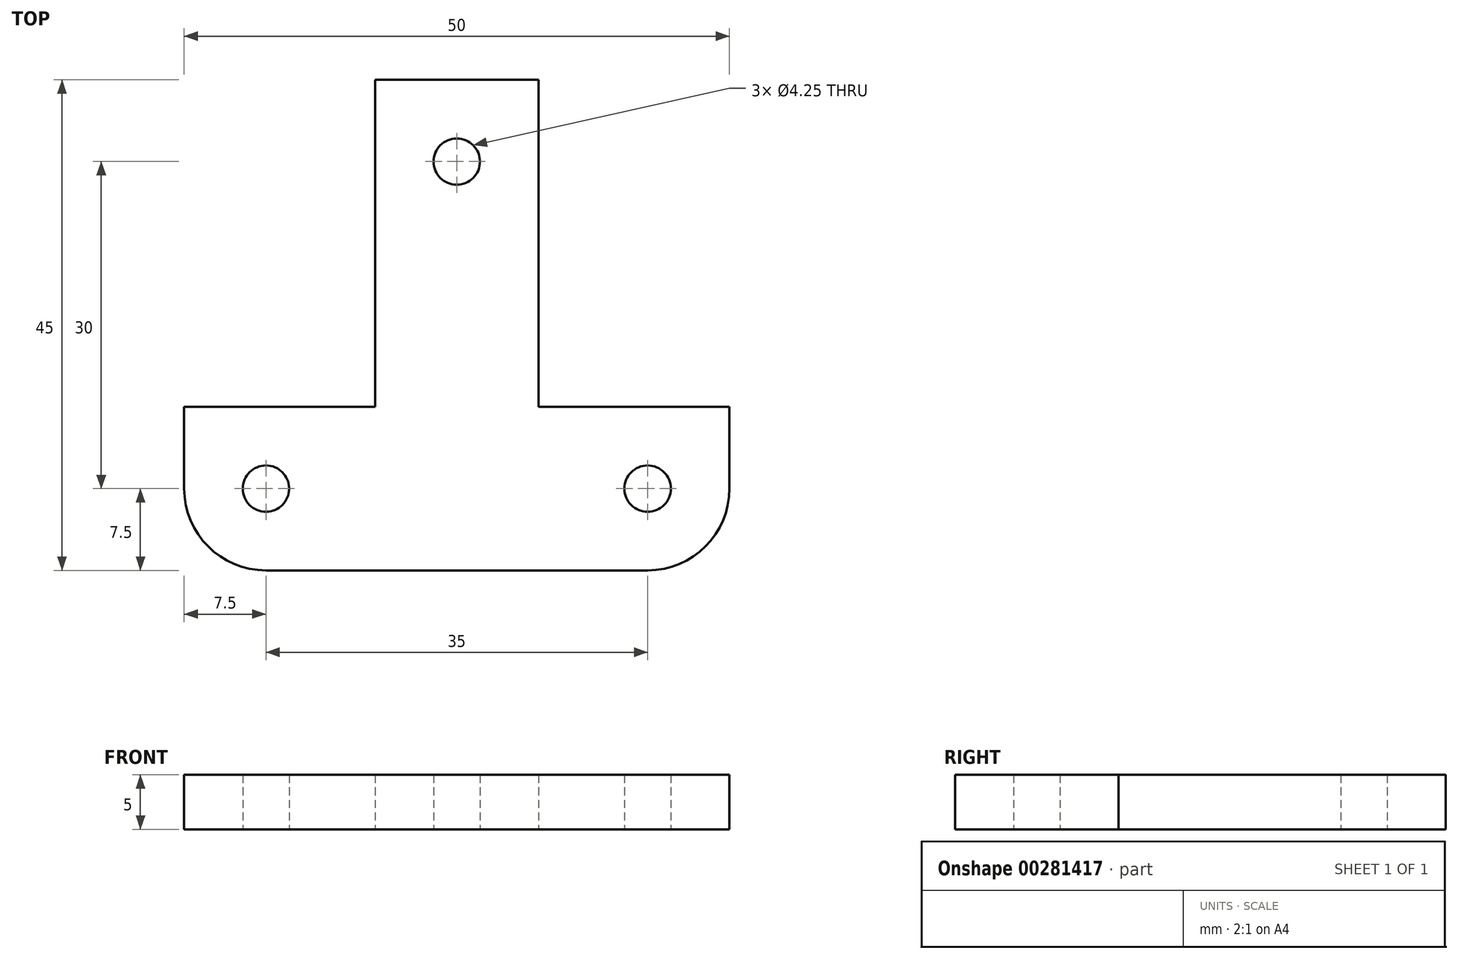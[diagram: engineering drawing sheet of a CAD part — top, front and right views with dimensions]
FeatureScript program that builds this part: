
annotation { "Feature Type Name" : "Feature", "Feature Type Description" : "" }
export const myFeature = defineFeature(function(context is Context, id is Id, definition is map)
    precondition{}
    {
        {
            var Q0;
            Q0=qCreatedBy(makeId("Top.planeOp"),FACE);
            var sketch = newSketch(context, id + "F0", { "sketchPlane" : qUnion([Q0])});
            skLineSegment(sketch, "E0", {"start": v(0, 37.5) * mm, "end": v(7.5, 37.5) * mm});
            skLineSegment(sketch, "E1", {"start": v(7.5, 37.5) * mm, "end": v(7.5, 7.5) * mm});
            skLineSegment(sketch, "E2", {"start": v(7.5, 7.5) * mm, "end": v(25, 7.5) * mm});
            skLineSegment(sketch, "E3", {"start": v(25, 7.5) * mm, "end": v(25, 0) * mm});
            skLineSegment(sketch, "E4.MirrorCS", {"start": v(0, 37.5) * mm, "end": v(-7.5, 37.5) * mm});
            skLineSegment(sketch, "E5.MirrorCS", {"start": v(-7.5, 37.5) * mm, "end": v(-7.5, 7.5) * mm});
            skLineSegment(sketch, "E6.MirrorCS", {"start": v(-7.5, 7.5) * mm, "end": v(-25, 7.5) * mm});
            skLineSegment(sketch, "E7.MirrorCS", {"start": v(-25, 7.5) * mm, "end": v(-25, 0) * mm});
            skLineSegment(sketch, "E8", {"start": v(-25, 0) * mm, "end": v(-25, -7.5) * mm});
            skLineSegment(sketch, "E9", {"start": v(-25, -7.5) * mm, "end": v(0, -7.5) * mm});
            skLineSegment(sketch, "E10.MirrorCS", {"start": v(25, -7.5) * mm, "end": v(0, -7.5) * mm});
            skLineSegment(sketch, "E11.MirrorCS", {"start": v(25, 0) * mm, "end": v(25, -7.5) * mm});
            skCircle(sketch, "E12", {"center": v(-17.5, 0) * mm, "radius": 2.12 * mm});
            skCircle(sketch, "E13", {"center": v(17.5, 0) * mm, "radius": 2.12 * mm});
            skCircle(sketch, "E14", {"center": v(0, 30) * mm, "radius": 2.12 * mm});
            skPoint(sketch, "E15.visualSharp", {"position": v(-7.5, 37.5) * mm});
            skLineSegment(sketch, "E15.filletArc", {"start": v(-7.5, 37.5) * mm, "end": v(-7.5, 37.5) * mm});
            skPoint(sketch, "E16.visualSharp", {"position": v(7.5, 37.5) * mm});
            skLineSegment(sketch, "E16.filletArc", {"start": v(7.5, 37.5) * mm, "end": v(7.5, 37.5) * mm});
            skPoint(sketch, "E17.visualSharp", {"position": v(-25, 7.5) * mm});
            skLineSegment(sketch, "E17.filletArc", {"start": v(-25, 7.5) * mm, "end": v(-25, 7.5) * mm});
            skPoint(sketch, "E18.visualSharp", {"position": v(-25, -7.5) * mm});
            skLineSegment(sketch, "E18.filletArc", {"start": v(-25, -7.5) * mm, "end": v(-25, -7.5) * mm});
            skPoint(sketch, "E19.visualSharp", {"position": v(25, -7.5) * mm});
            skLineSegment(sketch, "E19.filletArc", {"start": v(25, -7.5) * mm, "end": v(25, -7.5) * mm});
            skPoint(sketch, "E20.visualSharp", {"position": v(25, 7.5) * mm});
            skLineSegment(sketch, "E20.filletArc", {"start": v(25, 7.5) * mm, "end": v(25, 7.5) * mm});
            skSolve(sketch);
        }
        {
            var Q0;
            Q0=qSketchRegion(id+"F0",true);
            extrude(context, id + "F1", {"entities" : qUnion([Q0]), "depth" : 5 * mm});
        }
        {
            var Q0;
            Q0=makeQuery(id+"F1.opExtrude","SWEPT_EDGE",EDGE,{"disambiguationData":[OSD([sQuery(id+"F0.wireOp",EDGE,"E8"),sQuery(id+"F0.wireOp",EDGE,"E9")])]});
            var Q1;
            Q1=makeQuery(id+"F1.opExtrude","SWEPT_EDGE",EDGE,{"disambiguationData":[OSD([sQuery(id+"F0.wireOp",EDGE,"E10.MirrorCS"),sQuery(id+"F0.wireOp",EDGE,"E11.MirrorCS")])]});
            fillet(context, id + "F2", {"entities" : qUnion([Q0, Q1]), "radius" : 7.5 * mm, "tangentPropagation" : true, "allowEdgeOverflow" : false});
        }
    });
